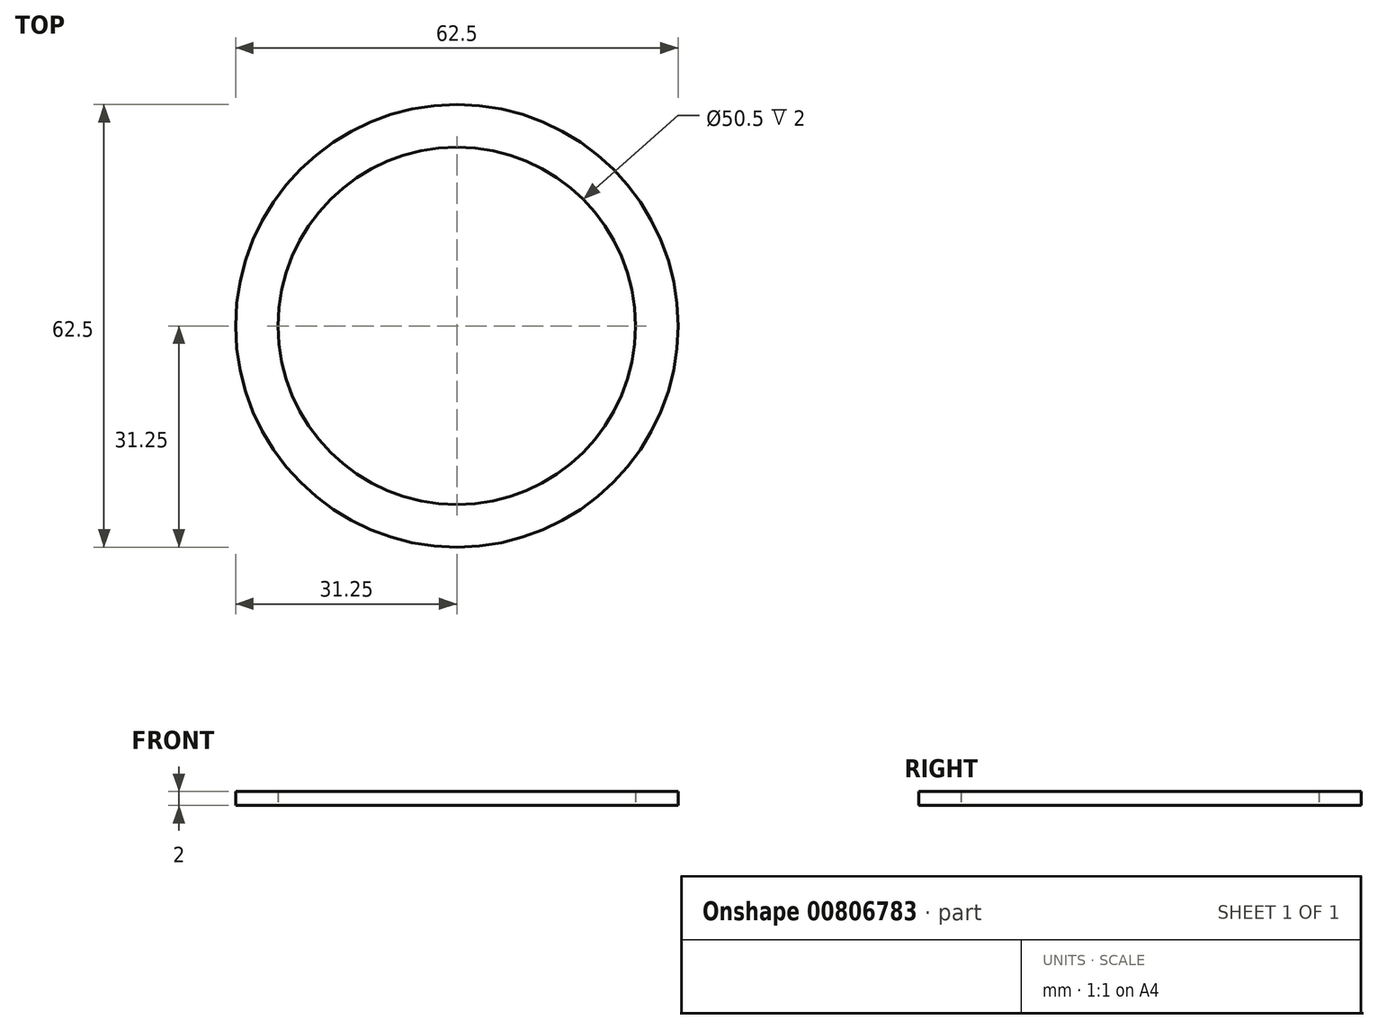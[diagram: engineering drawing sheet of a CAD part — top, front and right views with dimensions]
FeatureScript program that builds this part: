
annotation { "Feature Type Name" : "Feature", "Feature Type Description" : "" }
export const myFeature = defineFeature(function(context is Context, id is Id, definition is map)
    precondition{}
    {
        {
            var Q0;
            Q0=qCreatedBy(makeId("Top.planeOp"),FACE);
            var sketch = newSketch(context, id + "F0", { "sketchPlane" : qUnion([Q0])});
            skCircle(sketch, "E0", {"center": v(0, 0) * mm, "radius": 25.25 * mm});
            skCircle(sketch, "E1", {"center": v(0, 0) * mm, "radius": 31.25 * mm});
            skSolve(sketch);
        }
        {
            var Q0;
            Q0=makeQuery(id+"F0.imprint","IMPRINT",FACE,{"disambiguationData":[TD([[makeQuery(id+"F0.imprint","IMPRINT",EDGE,{"derivedFrom":sQuery(id+"F0.wireOp",EDGE,"E0")}),-1.0]])]});
            extrude(context, id + "F1", {"entities" : qUnion([Q0]), "depth" : 2 * mm, "offsetDistance" : 25 * mm});
        }
    });
